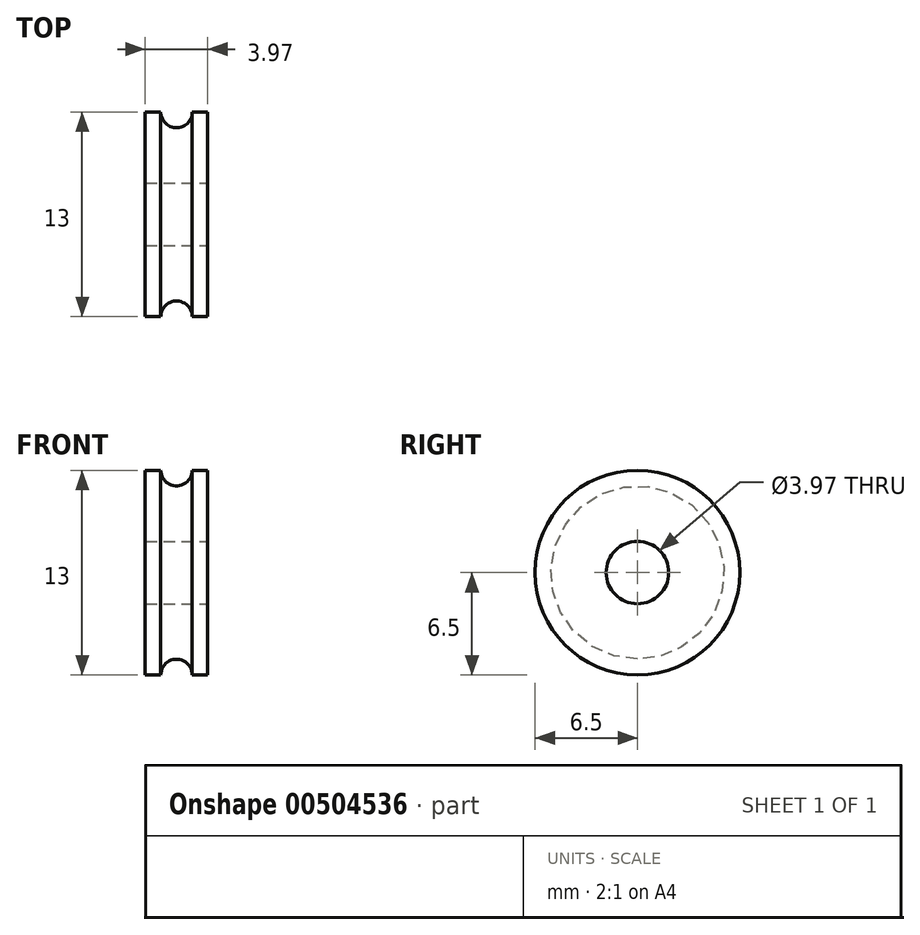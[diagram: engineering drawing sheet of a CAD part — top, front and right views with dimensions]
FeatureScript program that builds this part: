
annotation { "Feature Type Name" : "Feature", "Feature Type Description" : "" }
export const myFeature = defineFeature(function(context is Context, id is Id, definition is map)
    precondition{}
    {
        {
            var Q0;
            Q0=qCreatedBy(makeId("Front.planeOp"),FACE);
            var sketch = newSketch(context, id + "F0", { "sketchPlane" : qUnion([Q0])});
            skLineSegment(sketch, "E0", {"start": v(-3.97, 6.5) * mm, "end": v(-2.98, 6.5) * mm});
            skLineSegment(sketch, "E1", {"start": v(0, 6.5) * mm, "end": v(0, 1.98) * mm});
            skLineSegment(sketch, "E2", {"start": v(0, 1.98) * mm, "end": v(-3.97, 1.98) * mm});
            skLineSegment(sketch, "E3", {"start": v(-3.97, 6.5) * mm, "end": v(-3.97, 1.98) * mm});
            skLineSegment(sketch, "E4", {"start": v(0, 0) * mm, "end": v(-69.7, 0) * mm});
            skArc(sketch, "E5", {"start": v(-2.98, 6.5) * mm, "mid": v(-1.98, 5.5) * mm, "end": v(-0.98, 6.5) * mm});
            skLineSegment(sketch, "E6.trimOffspring", {"start": v(-0.98, 6.5) * mm, "end": v(0, 6.5) * mm});
            skSolve(sketch);
        }
        {
            var Q0;
            Q0=makeQuery(id+"F0.imprint","IMPRINT",FACE,{"disambiguationData":[TD([[makeQuery(id+"F0.imprint","IMPRINT",EDGE,{"derivedFrom":sQuery(id+"F0.wireOp",EDGE,"E0")}),-1.0]])]});
            var Q1;
            Q1=sQuery(id+"F0.wireOp",EDGE,"E4");
            revolve(context, id + "F1", {"entities" : qUnion([Q0]), "axis" : qUnion([Q1]), "revolveType" : RevolveType.FULL});
        }
    });
